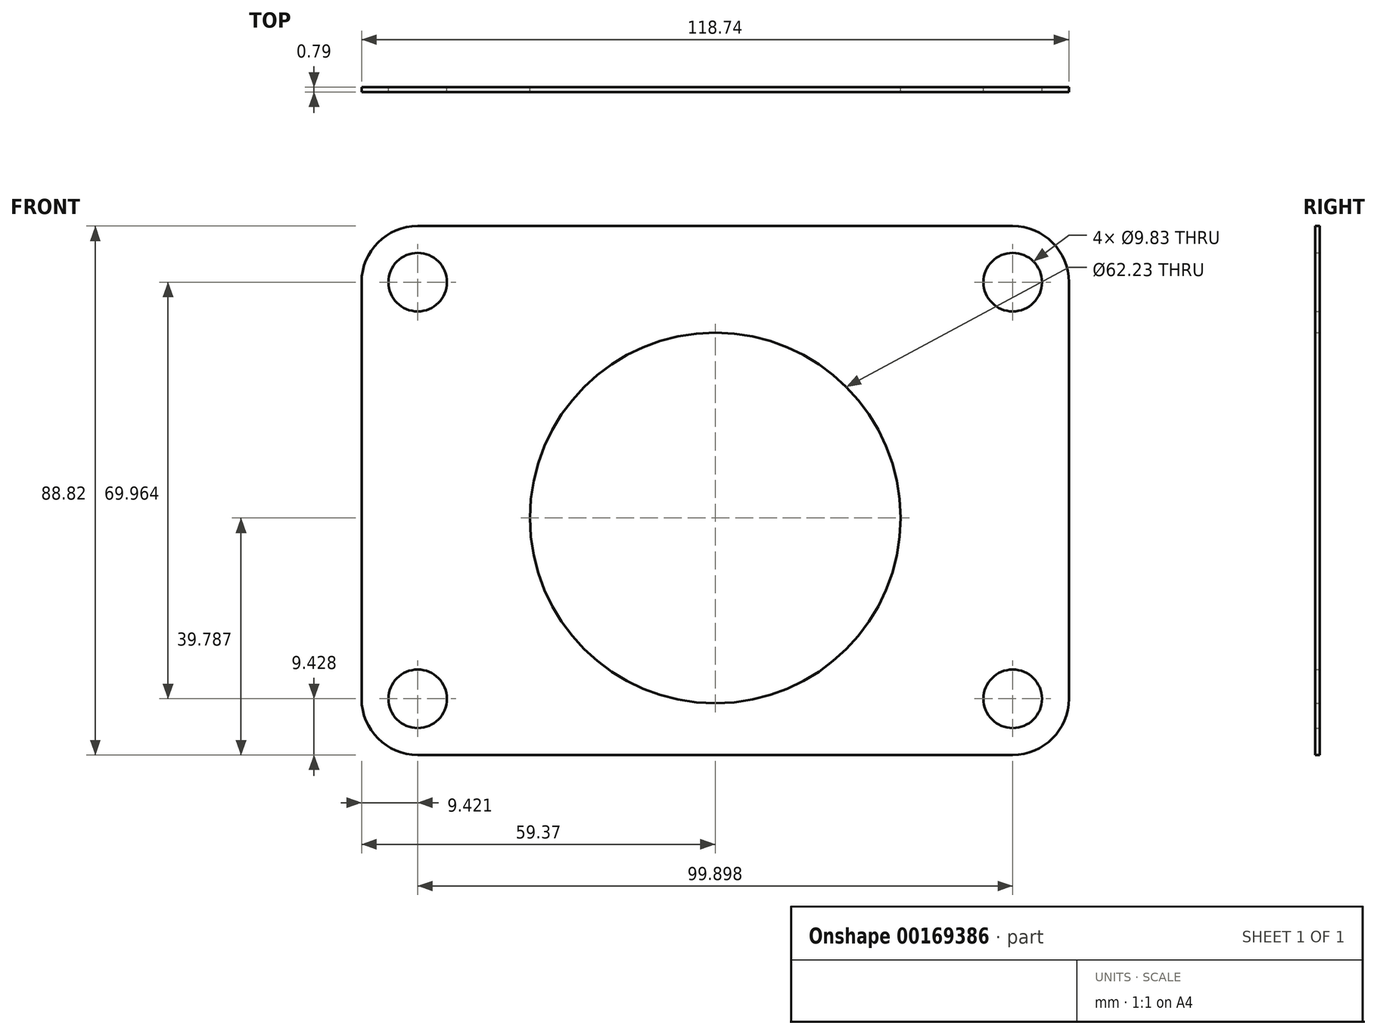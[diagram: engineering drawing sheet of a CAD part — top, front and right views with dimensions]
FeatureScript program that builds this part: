
annotation { "Feature Type Name" : "Feature", "Feature Type Description" : "" }
export const myFeature = defineFeature(function(context is Context, id is Id, definition is map)
    precondition{}
    {
        {
            var Q0;
            Q0=qCreatedBy(makeId("Front.planeOp"),FACE);
            var sketch = newSketch(context, id + "F0", { "sketchPlane" : qUnion([Q0])});
            skLineSegment(sketch, "E0.bottom", {"start": v(-49.95, 44.4) * mm, "end": v(49.95, 44.4) * mm});
            skLineSegment(sketch, "E0.top", {"start": v(-49.95, -44.4) * mm, "end": v(49.95, -44.4) * mm});
            skLineSegment(sketch, "E0.left", {"start": v(-59.37, 34.98) * mm, "end": v(-59.37, -34.98) * mm});
            skLineSegment(sketch, "E0.right", {"start": v(59.37, 34.98) * mm, "end": v(59.37, -34.98) * mm});
            skPoint(sketch, "E0.middle", {"position": v(0, 0) * mm});
            skLineSegment(sketch, "E1.bottom", {"start": v(-49.95, 34.98) * mm, "end": v(49.95, 34.98) * mm, "construction": true});
            skLineSegment(sketch, "E1.top", {"start": v(-49.95, -34.98) * mm, "end": v(49.95, -34.98) * mm, "construction": true});
            skLineSegment(sketch, "E1.left", {"start": v(-49.95, 34.98) * mm, "end": v(-49.95, -34.98) * mm, "construction": true});
            skLineSegment(sketch, "E1.right", {"start": v(49.95, 34.98) * mm, "end": v(49.95, -34.98) * mm, "construction": true});
            skCircle(sketch, "E2", {"center": v(-49.95, 34.98) * mm, "radius": 4.91 * mm});
            skCircle(sketch, "E3", {"center": v(49.95, 34.98) * mm, "radius": 4.91 * mm});
            skCircle(sketch, "E4", {"center": v(49.95, -34.98) * mm, "radius": 4.91 * mm});
            skCircle(sketch, "E5", {"center": v(-49.95, -34.98) * mm, "radius": 4.91 * mm});
            skCircle(sketch, "E6", {"center": v(-49.95, 34.98) * mm, "radius": 4.03 * mm, "construction": true});
            skCircle(sketch, "E7", {"center": v(-49.95, -34.98) * mm, "radius": 4.03 * mm, "construction": true});
            skCircle(sketch, "E8", {"center": v(49.95, -34.98) * mm, "radius": 4.03 * mm, "construction": true});
            skCircle(sketch, "E9", {"center": v(49.95, 34.98) * mm, "radius": 4.03 * mm, "construction": true});
            skPoint(sketch, "E10.visualSharp", {"position": v(-59.37, 44.4) * mm});
            skArc(sketch, "E10.filletArc", {"start": v(-49.95, 44.4) * mm, "mid": v(-56.61, 41.65) * mm, "end": v(-59.37, 34.98) * mm});
            skPoint(sketch, "E11.visualSharp", {"position": v(59.37, 44.4) * mm});
            skArc(sketch, "E11.filletArc", {"start": v(59.37, 34.98) * mm, "mid": v(56.61, 41.65) * mm, "end": v(49.95, 44.4) * mm});
            skPoint(sketch, "E12.visualSharp", {"position": v(59.37, -44.4) * mm});
            skArc(sketch, "E12.filletArc", {"start": v(49.95, -44.4) * mm, "mid": v(56.61, -41.65) * mm, "end": v(59.37, -34.98) * mm});
            skPoint(sketch, "E13.visualSharp", {"position": v(-59.37, -44.4) * mm});
            skArc(sketch, "E13.filletArc", {"start": v(-59.37, -34.98) * mm, "mid": v(-56.61, -41.65) * mm, "end": v(-49.95, -44.4) * mm});
            skCircle(sketch, "E14", {"center": v(0, -4.62) * mm, "radius": 28.58 * mm, "construction": true});
            skCircle(sketch, "E15", {"center": v(0, -4.62) * mm, "radius": 31.12 * mm});
            skSolve(sketch);
        }
        {
            var Q0;
            Q0 = qSketchRegion(id + "F0", true);
            extrude(context, id + "F1", {"entities" : qUnion([Q0]), "depth" : 0.8 * mm});
        }
    });
